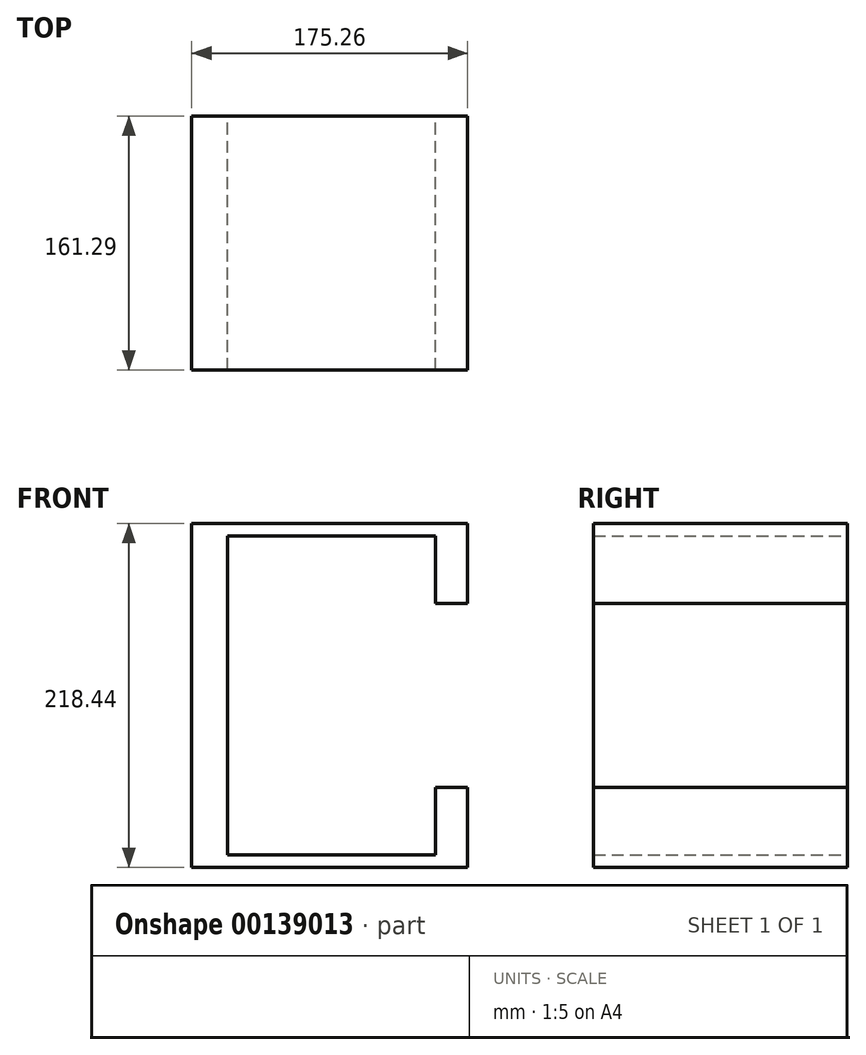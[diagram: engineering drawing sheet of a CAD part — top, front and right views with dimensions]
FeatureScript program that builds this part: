
annotation { "Feature Type Name" : "Feature", "Feature Type Description" : "" }
export const myFeature = defineFeature(function(context is Context, id is Id, definition is map)
    precondition{}
    {
        {
            var Q0;
            Q0=qCreatedBy(makeId("Front.planeOp"),FACE);
            var sketch = newSketch(context, id + "F0", { "sketchPlane" : qUnion([Q0])});
            skLineSegment(sketch, "E0", {"start": v(134.57, 176.1) * mm, "end": v(-40.7, 176.1) * mm});
            skLineSegment(sketch, "E1", {"start": v(-40.7, 176.1) * mm, "end": v(-40.7, -42.35) * mm});
            skLineSegment(sketch, "E2", {"start": v(-40.7, -42.35) * mm, "end": v(134.57, -42.35) * mm});
            skLineSegment(sketch, "E3", {"start": v(134.57, -42.35) * mm, "end": v(134.57, 8.45) * mm});
            skLineSegment(sketch, "E4", {"start": v(134.57, 8.45) * mm, "end": v(114.25, 8.45) * mm});
            skLineSegment(sketch, "E5", {"start": v(114.25, 8.45) * mm, "end": v(114.25, -34.35) * mm});
            skLineSegment(sketch, "E6", {"start": v(114.25, -34.35) * mm, "end": v(-17.83, -34.35) * mm});
            skLineSegment(sketch, "E7", {"start": v(-17.83, -34.35) * mm, "end": v(-17.83, 168.1) * mm});
            skLineSegment(sketch, "E8", {"start": v(-17.83, 168.1) * mm, "end": v(114.25, 168.1) * mm});
            skLineSegment(sketch, "E9", {"start": v(114.25, 168.1) * mm, "end": v(114.25, 125.3) * mm});
            skLineSegment(sketch, "E10", {"start": v(114.25, 125.3) * mm, "end": v(134.57, 125.3) * mm});
            skLineSegment(sketch, "E11", {"start": v(134.57, 125.3) * mm, "end": v(134.57, 176.1) * mm});
            skSolve(sketch);
        }
        {
            var Q0;
            Q0 = qSketchRegion(id + "F0", true);
            extrude(context, id + "F1", {"entities" : qUnion([Q0]), "depth" : 161.29 * mm});
        }
    });
